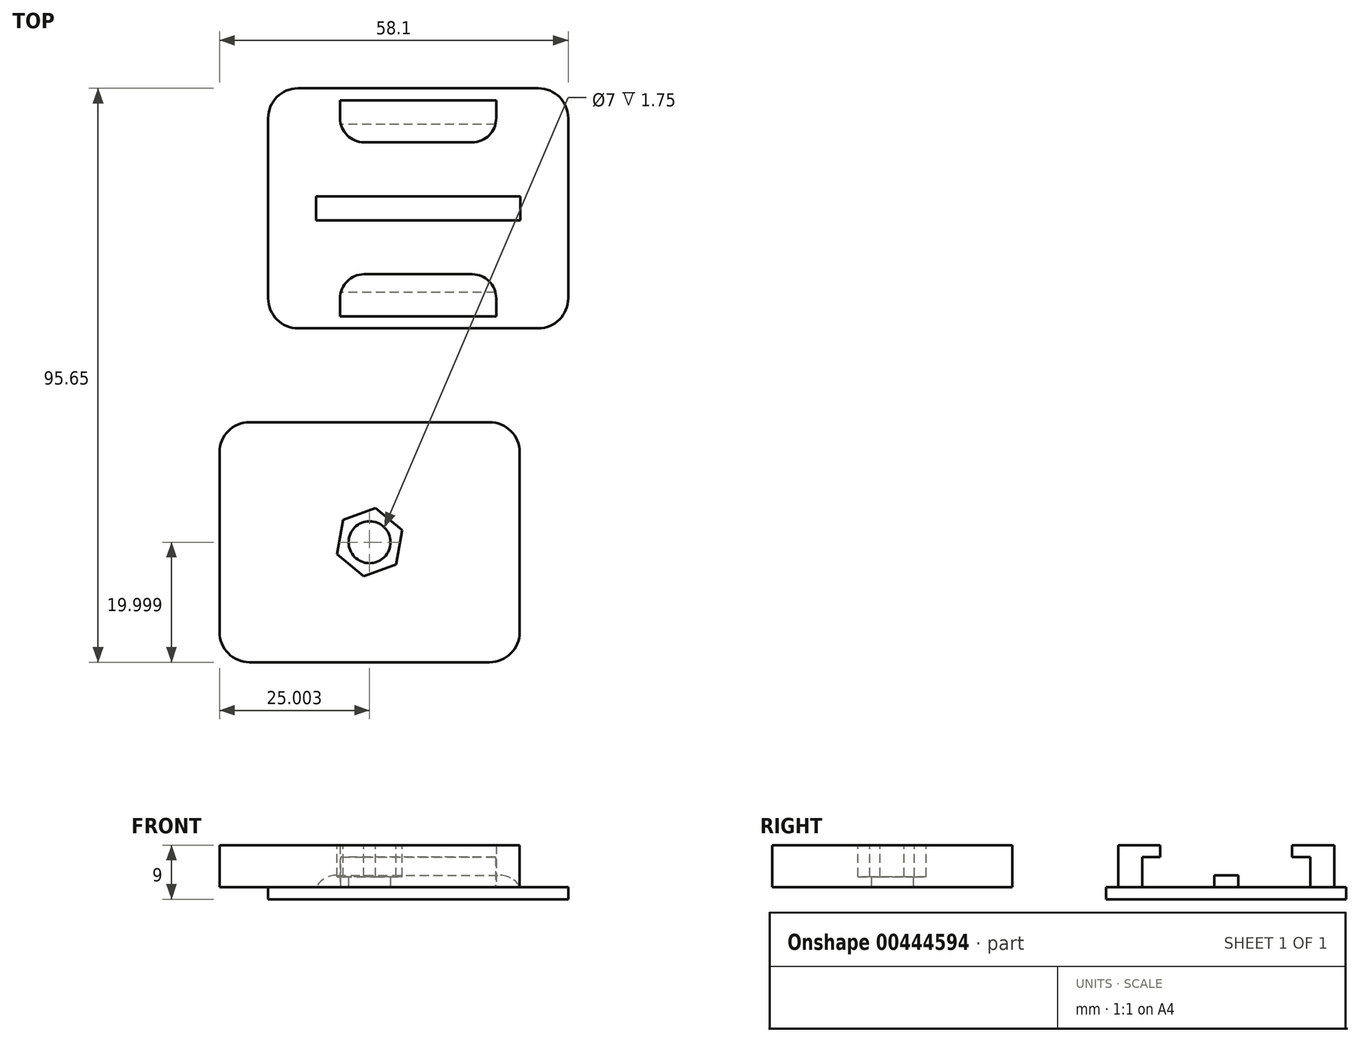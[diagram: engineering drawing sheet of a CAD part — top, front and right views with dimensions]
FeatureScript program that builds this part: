
annotation { "Feature Type Name" : "Feature", "Feature Type Description" : "" }
export const myFeature = defineFeature(function(context is Context, id is Id, definition is map)
    precondition{}
    {
        {
            var Q0;
            Q0=qCreatedBy(makeId("Top.planeOp"),FACE);
            var sketch = newSketch(context, id + "F0", { "sketchPlane" : qUnion([Q0])});
            skLineSegment(sketch, "E0.bottom", {"start": v(0, 0) * mm, "end": v(-26, 0) * mm});
            skLineSegment(sketch, "E0.top", {"start": v(0, 4) * mm, "end": v(-26, 4) * mm});
            skLineSegment(sketch, "E0.left", {"start": v(0, 0) * mm, "end": v(0, 4) * mm});
            skLineSegment(sketch, "E0.right", {"start": v(-26, 0) * mm, "end": v(-26, 4) * mm});
            skLineSegment(sketch, "E1.bottom", {"start": v(0, 32) * mm, "end": v(-26, 32) * mm});
            skLineSegment(sketch, "E1.top", {"start": v(0, 36) * mm, "end": v(-26, 36) * mm});
            skLineSegment(sketch, "E1.left", {"start": v(0, 32) * mm, "end": v(0, 36) * mm});
            skLineSegment(sketch, "E1.right", {"start": v(-26, 32) * mm, "end": v(-26, 36) * mm});
            skSolve(sketch);
        }
        {
            var Q0;
            Q0 = qSketchRegion(id + "F0", true);
            extrude(context, id + "F1", {"entities" : qUnion([Q0]), "depth" : 5 * mm});
        }
        {
            var Q0;
            Q0=makeQuery(id+"F1.opExtrude","CAP_FACE",FACE,{"disambiguationData":[OSD([sQuery(id+"F0.wireOp",EDGE,"E0.bottom"),sQuery(id+"F0.wireOp",EDGE,"E0.top"),sQuery(id+"F0.wireOp",EDGE,"E0.left"),sQuery(id+"F0.wireOp",EDGE,"E0.right")])],"isStart":false});
            var sketch = newSketch(context, id + "F2", { "sketchPlane" : qUnion([Q0])});
            skLineSegment(sketch, "E2.bottom", {"start": v(0, 0) * mm, "end": v(-26, 0) * mm});
            skLineSegment(sketch, "E2.top", {"start": v(0, 7) * mm, "end": v(-26, 7) * mm});
            skLineSegment(sketch, "E2.left", {"start": v(0, 0) * mm, "end": v(0, 7) * mm});
            skLineSegment(sketch, "E2.right", {"start": v(-26, 0) * mm, "end": v(-26, 7) * mm});
            skLineSegment(sketch, "E3.bottom", {"start": v(-26, 36) * mm, "end": v(0, 36) * mm});
            skLineSegment(sketch, "E3.top", {"start": v(-26, 29) * mm, "end": v(0, 29) * mm});
            skLineSegment(sketch, "E3.left", {"start": v(-26, 36) * mm, "end": v(-26, 29) * mm});
            skLineSegment(sketch, "E3.right", {"start": v(0, 36) * mm, "end": v(0, 29) * mm});
            skSolve(sketch);
        }
        {
            var Q0;
            Q0 = qSketchRegion(id + "F2", true);
            extrude(context, id + "F3", {"entities" : qUnion([Q0]), "operationType" : NewBodyOperationType.ADD, "depth" : 2 * mm});
        }
        {
            var Q0;
            Q0=qCreatedBy(makeId("Top.planeOp"),FACE);
            var sketch = newSketch(context, id + "F4", { "sketchPlane" : qUnion([Q0])});
            skLineSegment(sketch, "E4.bottom", {"start": v(-30, 20) * mm, "end": v(4, 20) * mm});
            skLineSegment(sketch, "E4.top", {"start": v(-30, 16) * mm, "end": v(4, 16) * mm});
            skLineSegment(sketch, "E4.left", {"start": v(-30, 20) * mm, "end": v(-30, 16) * mm});
            skLineSegment(sketch, "E4.right", {"start": v(4, 20) * mm, "end": v(4, 16) * mm});
            skSolve(sketch);
        }
        {
            var Q0;
            Q0 = qSketchRegion(id + "F4", true);
            extrude(context, id + "F5", {"entities" : qUnion([Q0]), "depth" : 2 * mm});
        }
        {
            var Q0;
            Q0=qCreatedBy(makeId("Top.planeOp"),FACE);
            var sketch = newSketch(context, id + "F6", { "sketchPlane" : qUnion([Q0])});
            skLineSegment(sketch, "E5.bottom", {"start": v(-38, 38) * mm, "end": v(12, 38) * mm});
            skLineSegment(sketch, "E5.top", {"start": v(-38, -2) * mm, "end": v(12, -2) * mm});
            skLineSegment(sketch, "E5.left", {"start": v(-38, 38) * mm, "end": v(-38, -2) * mm});
            skLineSegment(sketch, "E5.right", {"start": v(12, 38) * mm, "end": v(12, -2) * mm});
            skSolve(sketch);
        }
        {
            var Q0;
            Q0 = qSketchRegion(id + "F6", true);
            extrude(context, id + "F7", {"entities" : qUnion([Q0]), "oppositeDirection" : true, "depth" : 2 * mm});
        }
        {
            var Q0;
            Q0=qCreatedBy(makeId("Top.planeOp"),FACE);
            var sketch = newSketch(context, id + "F8", { "sketchPlane" : qUnion([Q0])});
            skLineSegment(sketch, "E6.bottom", {"start": v(-46.1, -17.65) * mm, "end": v(3.9, -17.65) * mm});
            skLineSegment(sketch, "E6.top", {"start": v(-46.1, -57.65) * mm, "end": v(3.9, -57.65) * mm});
            skLineSegment(sketch, "E6.left", {"start": v(-46.1, -17.65) * mm, "end": v(-46.1, -57.65) * mm});
            skLineSegment(sketch, "E6.right", {"start": v(3.9, -17.65) * mm, "end": v(3.9, -57.65) * mm});
            skSolve(sketch);
        }
        {
            var Q0;
            Q0 = qSketchRegion(id + "F8", true);
            extrude(context, id + "F9", {"entities" : qUnion([Q0]), "depth" : 7 * mm});
        }
        {
            var Q0;
            Q0=makeQuery(id+"F9.opExtrude","CAP_FACE",FACE,{"disambiguationData":[OSD([sQuery(id+"F8.wireOp",EDGE,"E6.bottom"),sQuery(id+"F8.wireOp",EDGE,"E6.top"),sQuery(id+"F8.wireOp",EDGE,"E6.left"),sQuery(id+"F8.wireOp",EDGE,"E6.right")])],"isStart":false});
            var sketch = newSketch(context, id + "F10", { "sketchPlane" : qUnion([Q0])});
            skCircle(sketch, "E7.cCircle", {"center": v(-21.1, -37.65) * mm, "radius": 5 * mm, "construction": true});
            skPoint(sketch, "E7.cCircle.centerSnap0", {"position": v(-46.1, -37.65) * mm});
            skPoint(sketch, "E7.cCircle.centerSnap1", {"position": v(-21.1, -17.65) * mm});
            skLineSegment(sketch, "E7.0", {"start": v(-25.53, -33.95) * mm, "end": v(-20.11, -31.96) * mm});
            skLineSegment(sketch, "E7.1", {"start": v(-20.11, -31.96) * mm, "end": v(-15.68, -35.66) * mm});
            skLineSegment(sketch, "E7.2", {"start": v(-15.68, -35.66) * mm, "end": v(-16.66, -41.35) * mm});
            skLineSegment(sketch, "E7.3", {"start": v(-16.66, -41.35) * mm, "end": v(-22.08, -43.34) * mm});
            skLineSegment(sketch, "E7.4", {"start": v(-22.08, -43.34) * mm, "end": v(-26.52, -39.64) * mm});
            skLineSegment(sketch, "E7.5", {"start": v(-26.52, -39.64) * mm, "end": v(-25.53, -33.95) * mm});
            skPoint(sketch, "E7.0.midPoint", {"position": v(-22.82, -32.96) * mm});
            skSolve(sketch);
        }
        {
            var Q0;
            Q0=makeQuery(id+"F9.opExtrude","CAP_FACE",FACE,{"disambiguationData":[OSD([sQuery(id+"F8.wireOp",EDGE,"E6.bottom"),sQuery(id+"F8.wireOp",EDGE,"E6.top"),sQuery(id+"F8.wireOp",EDGE,"E6.left"),sQuery(id+"F8.wireOp",EDGE,"E6.right")])],"isStart":true});
            var sketch = newSketch(context, id + "F11", { "sketchPlane" : qUnion([Q0])});
            skCircle(sketch, "E8", {"center": v(-21.1, 37.65) * mm, "radius": 3.5 * mm});
            skPoint(sketch, "E8.centerSnap0", {"position": v(-46.1, 37.65) * mm});
            skPoint(sketch, "E8.centerSnap1", {"position": v(-21.1, 57.65) * mm});
            skSolve(sketch);
        }
        {
            var Q0;
            Q0 = qSketchRegion(id + "F11", true);
            extrude(context, id + "F12", {"entities" : qUnion([Q0]), "operationType" : NewBodyOperationType.REMOVE, "endBound" : BoundingType.THROUGH_ALL, "oppositeDirection" : true, "depth" : 25 * mm});
        }
        {
            var Q0;
            Q0 = qSketchRegion(id + "F10", true);
            extrude(context, id + "F13", {"entities" : qUnion([Q0]), "operationType" : NewBodyOperationType.REMOVE, "oppositeDirection" : true, "depth" : 5.25 * mm});
        }
        {
            var Q0;
            Q0=makeQuery(id+"F3.opExtrude","SWEPT_EDGE",EDGE,{"disambiguationData":[OSD([sQuery(id+"F2.wireOp",EDGE,"E3.top"),sQuery(id+"F2.wireOp",EDGE,"E3.right")])]});
            var Q1;
            Q1=makeQuery(id+"F3.opExtrude","SWEPT_EDGE",EDGE,{"disambiguationData":[OSD([sQuery(id+"F2.wireOp",EDGE,"E3.top"),sQuery(id+"F2.wireOp",EDGE,"E3.left")])]});
            var Q2;
            Q2=makeQuery(id+"F3.opExtrude","SWEPT_EDGE",EDGE,{"disambiguationData":[OSD([sQuery(id+"F2.wireOp",EDGE,"E2.top"),sQuery(id+"F2.wireOp",EDGE,"E2.left")])]});
            var Q3;
            Q3=makeQuery(id+"F5.opExtrude","CAP_EDGE",EDGE,{"disambiguationData":[OSD([sQuery(id+"F4.wireOp",EDGE,"E4.right")])],"isStart":false});
            var Q4;
            Q4=makeQuery(id+"F3.opExtrude","SWEPT_EDGE",EDGE,{"disambiguationData":[OSD([sQuery(id+"F2.wireOp",EDGE,"E2.top"),sQuery(id+"F2.wireOp",EDGE,"E2.right")])]});
            var Q5;
            Q5=makeQuery(id+"F5.opExtrude","CAP_EDGE",EDGE,{"disambiguationData":[OSD([sQuery(id+"F4.wireOp",EDGE,"E4.left")])],"isStart":false});
            fillet(context, id + "F14", {"entities" : qUnion([Q0, Q1, Q2, Q3, Q4, Q5]), "radius" : 4 * mm, "tangentPropagation" : true, "allowEdgeOverflow" : false});
        }
        {
            var Q0;
            Q0=makeQuery(id+"F7.opExtrude","SWEPT_EDGE",EDGE,{"disambiguationData":[OSD([sQuery(id+"F6.wireOp",EDGE,"E5.top"),sQuery(id+"F6.wireOp",EDGE,"E5.right")])]});
            var Q1;
            Q1=makeQuery(id+"F7.opExtrude","SWEPT_EDGE",EDGE,{"disambiguationData":[OSD([sQuery(id+"F6.wireOp",EDGE,"E5.bottom"),sQuery(id+"F6.wireOp",EDGE,"E5.right")])]});
            var Q2;
            Q2=makeQuery(id+"F7.opExtrude","SWEPT_EDGE",EDGE,{"disambiguationData":[OSD([sQuery(id+"F6.wireOp",EDGE,"E5.top"),sQuery(id+"F6.wireOp",EDGE,"E5.left")])]});
            var Q3;
            Q3=makeQuery(id+"F7.opExtrude","SWEPT_EDGE",EDGE,{"disambiguationData":[OSD([sQuery(id+"F6.wireOp",EDGE,"E5.bottom"),sQuery(id+"F6.wireOp",EDGE,"E5.left")])]});
            fillet(context, id + "F15", {"entities" : qUnion([Q0, Q1, Q2, Q3]), "radius" : 5 * mm, "tangentPropagation" : true, "allowEdgeOverflow" : false});
        }
        {
            var Q0;
            Q0=makeQuery(id+"F9.opExtrude","SWEPT_EDGE",EDGE,{"disambiguationData":[OSD([sQuery(id+"F8.wireOp",EDGE,"E6.bottom"),sQuery(id+"F8.wireOp",EDGE,"E6.left")])]});
            var Q1;
            Q1=makeQuery(id+"F9.opExtrude","SWEPT_EDGE",EDGE,{"disambiguationData":[OSD([sQuery(id+"F8.wireOp",EDGE,"E6.bottom"),sQuery(id+"F8.wireOp",EDGE,"E6.right")])]});
            var Q2;
            Q2=makeQuery(id+"F9.opExtrude","SWEPT_EDGE",EDGE,{"disambiguationData":[OSD([sQuery(id+"F8.wireOp",EDGE,"E6.top"),sQuery(id+"F8.wireOp",EDGE,"E6.left")])]});
            var Q3;
            Q3=makeQuery(id+"F9.opExtrude","SWEPT_EDGE",EDGE,{"disambiguationData":[OSD([sQuery(id+"F8.wireOp",EDGE,"E6.top"),sQuery(id+"F8.wireOp",EDGE,"E6.right")])]});
            fillet(context, id + "F16", {"entities" : qUnion([Q0, Q1, Q2, Q3]), "radius" : 5 * mm, "tangentPropagation" : true, "allowEdgeOverflow" : false});
        }
    });
